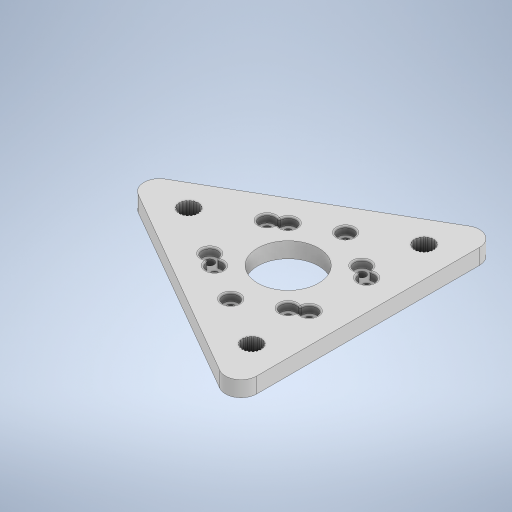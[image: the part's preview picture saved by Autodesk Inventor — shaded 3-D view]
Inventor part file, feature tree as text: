
AUTODESK INVENTOR PART (.ipt)
format: ipt  version: 2024 (Build 280153000, 153)  size: 592,896 bytes
history: native  units: in
note: dims shown in document units (in); Inventor stores cm internally (conversion verified against a paired STEP export)
features: extrude x3, fillet x2, sketch x1
ambient origin geometry x8: Origin, YZ Plane, XZ Plane, XY Plane, X Axis, Y Axis, Z Axis, Center Point
bodies: Solid1 (feature_tree)
feature tree (6):
  extrude  "Extrusion1"  Depth=0.0394in
  fillet  "Fillet1"  Radius=4.0415in
  sketch  "Sketch3"  dims[d0=7.0in d1=1.5394in d2=4.0415in d3=2.5161in d4=0.481in d5=120.0deg d6=120.0deg d7=0.3937in d8=0.0in d9=0.3937in d11=0.0203in d12=0.2407in d13=7.874in d15=360.0deg d17=1.1811in d19=360.0deg d21=0.2047in d22=0.2047in d23=1.8638in d24=1.8638in d25=0.9319in d26=0.9319in d27=0.2165in d28=4.358in d29=1.4527in d30=1.4527in d31=1.4527in d32=1.4527in d33=1.4527in d34=1.4527in d35=0.3937in d36=0.0in d37=0.3937in d38=0.3937in d39=0.3937in d40=0.3937in d41=0.3937in d42=0.3937in d43=0.3937in d44=0.3937in d45=0.3937in d46=0.3937in d47=0.1969in d48=0.0in d49=0.0394in]
  extrude  "Extrusion2"  Depth=0.0394in
  extrude  "Extrusion3"  Depth=0.0394in
  fillet  "Fillet2"  [1 undecoded]
note: 1 required parameter value undecoded (feature->parameter linkage not recoverable at this tier; creation-order binding heuristic only, values carry confidence <= 0.55)
